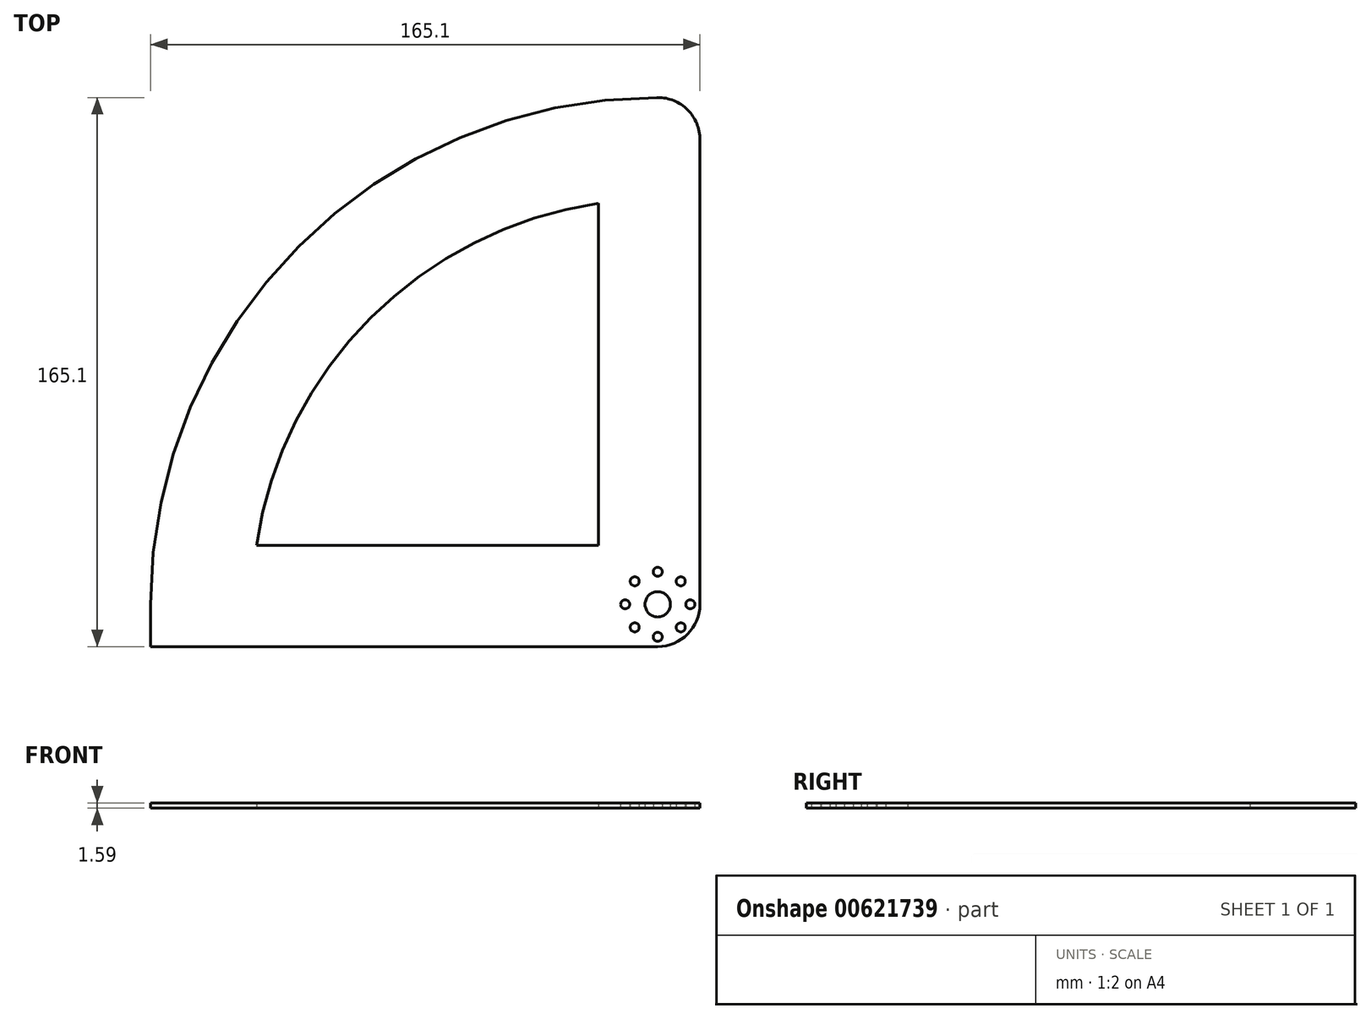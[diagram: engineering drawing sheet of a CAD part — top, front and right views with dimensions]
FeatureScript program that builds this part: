
annotation { "Feature Type Name" : "Feature", "Feature Type Description" : "" }
export const myFeature = defineFeature(function(context is Context, id is Id, definition is map)
    precondition{}
    {
        {
            var Q0;
            Q0=qCreatedBy(makeId("Top.planeOp"),FACE);
            var sketch = newSketch(context, id + "F0", { "sketchPlane" : qUnion([Q0])});
            skLineSegment(sketch, "E0.bottom", {"start": v(0, 0) * mm, "end": v(165.1, 0) * mm});
            skLineSegment(sketch, "E0.top", {"start": v(164.82, 165.1) * mm, "end": v(165.1, 165.1) * mm});
            skLineSegment(sketch, "E0.left", {"start": v(0, 0) * mm, "end": v(0, 0) * mm});
            skLineSegment(sketch, "E0.right", {"start": v(165.1, 0) * mm, "end": v(165.1, 165.1) * mm});
            skLineSegment(sketch, "E1", {"start": v(165.1, 0) * mm, "end": v(165.1, 25.4) * mm});
            skLineSegment(sketch, "E2", {"start": v(152.12, 165.1) * mm, "end": v(164.82, 165.1) * mm});
            skLineSegment(sketch, "E3", {"start": v(0, 0) * mm, "end": v(0, 12.7) * mm});
            skArc(sketch, "E4", {"start": v(152.12, 165.1) * mm, "mid": v(44.54, 120.36) * mm, "end": v(0, 12.7) * mm});
            skLineSegment(sketch, "E5.bottom", {"start": v(165.1, 0) * mm, "end": v(0, 0) * mm});
            skLineSegment(sketch, "E5.top", {"start": v(165.1, 165.1) * mm, "end": v(152.4, 165.1) * mm});
            skArc(sketch, "E6.0", {"start": v(134.62, 133.32) * mm, "mid": v(66.19, 98.91) * mm, "end": v(31.78, 30.48) * mm});
            skLineSegment(sketch, "E7", {"start": v(31.78, 30.48) * mm, "end": v(134.62, 30.48) * mm});
            skLineSegment(sketch, "E8", {"start": v(134.62, 30.48) * mm, "end": v(134.62, 133.32) * mm});
            skCircle(sketch, "E9", {"center": v(152.4, 12.7) * mm, "radius": 3.8 * mm});
            skCircle(sketch, "E10", {"center": v(159.32, 19.62) * mm, "radius": 1.36 * mm});
            skCircle(sketch, "E11.1.0", {"center": v(152.4, 22.49) * mm, "radius": 1.36 * mm});
            skCircle(sketch, "E11.2.0", {"center": v(145.48, 19.62) * mm, "radius": 1.36 * mm});
            skCircle(sketch, "E12.1.3.0", {"center": v(142.61, 12.7) * mm, "radius": 1.36 * mm});
            skCircle(sketch, "E12.1.4.0", {"center": v(145.48, 5.78) * mm, "radius": 1.36 * mm});
            skCircle(sketch, "E12.1.5.0", {"center": v(152.4, 2.91) * mm, "radius": 1.36 * mm});
            skCircle(sketch, "E12.1.6.0", {"center": v(159.32, 5.78) * mm, "radius": 1.36 * mm});
            skCircle(sketch, "E12.1.7.0", {"center": v(162.19, 12.7) * mm, "radius": 1.36 * mm});
            skLineSegment(sketch, "E13", {"start": v(152.4, 12.7) * mm, "end": v(152.4, 22.49) * mm, "construction": true});
            skSolve(sketch);
        }
        {
            var Q0;
            {var subQ1=sQuery(id+"F0.wireOp",EDGE,"E2");Q0=makeQuery(id+"F0.imprint","IMPRINT",FACE,{"disambiguationData":[TD([[makeQuery(id+"F0.imprint","IMPRINT",EDGE,{"derivedFrom":subQ1}),-1.0]])]});}
            extrude(context, id + "F1", {"entities" : qUnion([Q0]), "depth" : 1.59 * mm, "offsetDistance" : 25.4 * mm});
        }
        {
            var Q0;
            Q0=makeQuery(id+"F1.opExtrude","SWEPT_EDGE",EDGE,{"disambiguationData":[OSD([sQuery(id+"F0.wireOp",EDGE,"E5.bottom"),sQuery(id+"F0.wireOp",EDGE,"E0.right")])]});
            fillet(context, id + "F2", {"entities" : qUnion([Q0]), "radius" : 12.7 * mm, "tangentPropagation" : true, "allowEdgeOverflow" : false});
        }
    });
